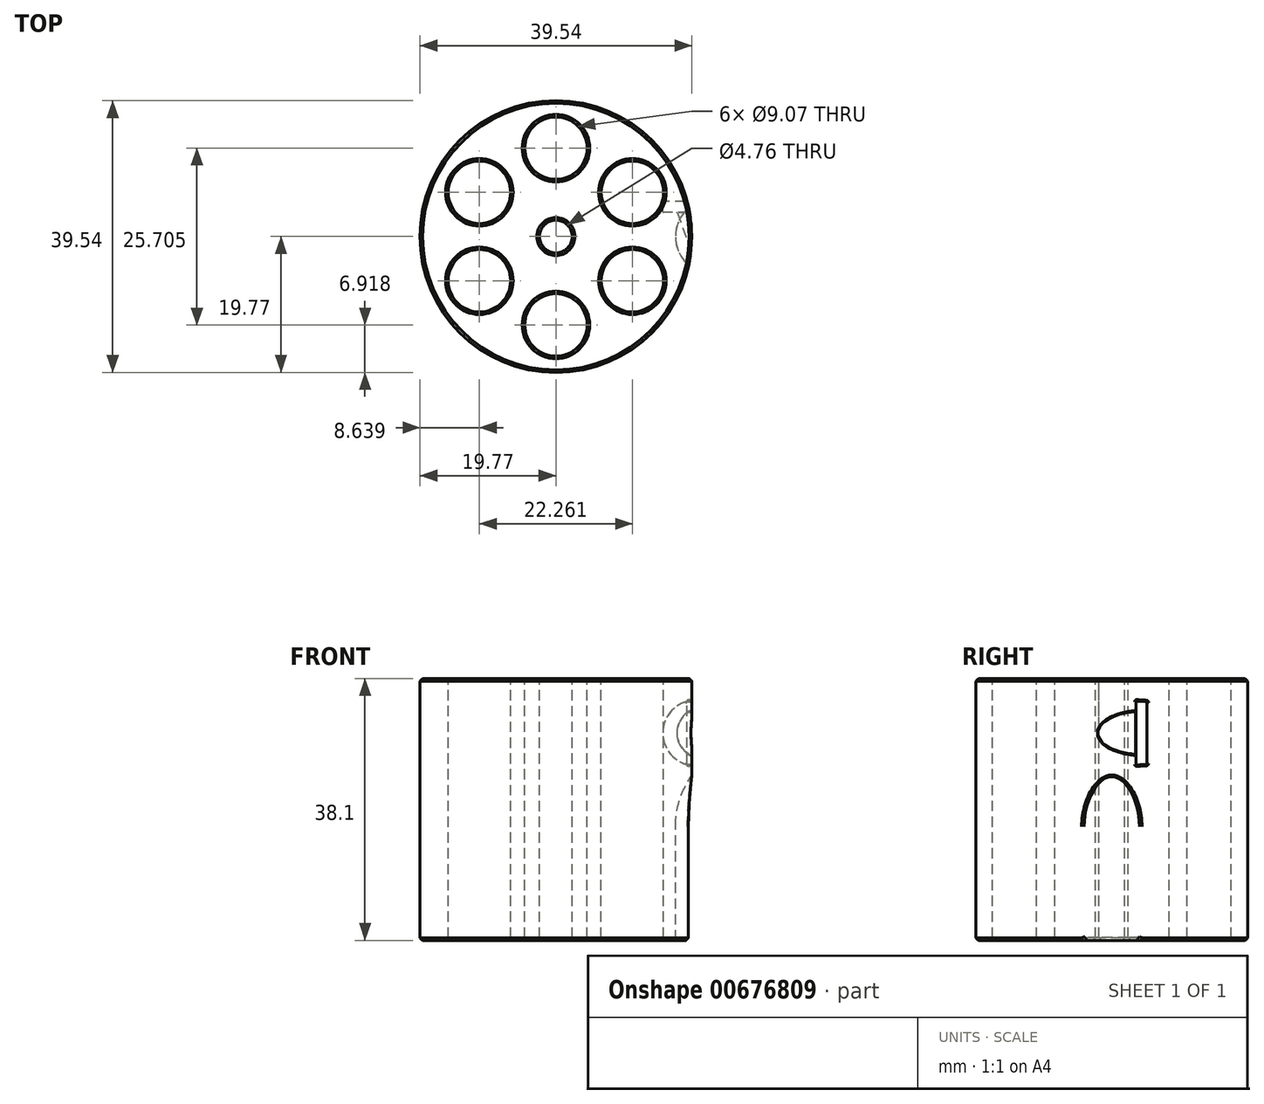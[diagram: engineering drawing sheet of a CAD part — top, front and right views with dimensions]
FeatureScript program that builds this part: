
annotation { "Feature Type Name" : "Feature", "Feature Type Description" : "" }
export const myFeature = defineFeature(function(context is Context, id is Id, definition is map)
    precondition{}
    {
        {
            var Q0;
            Q0=qCreatedBy(makeId("Top.planeOp"),FACE);
            var sketch = newSketch(context, id + "F0", { "sketchPlane" : qUnion([Q0])});
            skCircle(sketch, "E0", {"center": v(0, 0) * mm, "radius": 19.77 * mm});
            skCircle(sketch, "E1", {"center": v(0, 12.85) * mm, "radius": 4.53 * mm});
            skCircle(sketch, "E2", {"center": v(0, 0) * mm, "radius": 12.85 * mm, "construction": true});
            skCircle(sketch, "E3.1.0", {"center": v(-11.13, 6.43) * mm, "radius": 4.53 * mm});
            skCircle(sketch, "E3.2.0", {"center": v(-11.13, -6.43) * mm, "radius": 4.53 * mm});
            skCircle(sketch, "E4.1.3.0", {"center": v(0, -12.85) * mm, "radius": 4.53 * mm});
            skCircle(sketch, "E4.1.4.0", {"center": v(11.13, -6.43) * mm, "radius": 4.53 * mm});
            skCircle(sketch, "E4.1.5.0", {"center": v(11.13, 6.43) * mm, "radius": 4.53 * mm});
            skCircle(sketch, "E5", {"center": v(0, 18.58) * mm, "radius": 1.2 * mm, "construction": true});
            skCircle(sketch, "E6", {"center": v(0, 0) * mm, "radius": 2.38 * mm});
            skSolve(sketch);
        }
        {
            var Q0;
            Q0 = qSketchRegion(id + "F0", true);
            extrude(context, id + "F1", {"entities" : qUnion([Q0]), "oppositeDirection" : true, "depth" : 38.1 * mm, "offsetDistance" : 25.4 * mm});
        }
        {
            var Q0;
            Q0=makeQuery(id+"F1.opExtrude","CAP_EDGE",EDGE,{"disambiguationData":[OSD([sQuery(id+"F0.wireOp",EDGE,"E0")])],"isStart":true});
            var Q1;
            Q1=makeQuery(id+"F1.opExtrude","CAP_EDGE",EDGE,{"disambiguationData":[OSD([sQuery(id+"F0.wireOp",EDGE,"E0")])],"isStart":false});
            chamfer(context, id + "F2", {"entities" : qUnion([Q0, Q1]), "width" : 0.38 * mm, "tangentPropagation" : true});
        }
        {
            var Q0;
            Q0=makeQuery(id+"F1.opExtrude","CAP_EDGE",EDGE,{"disambiguationData":[OSD([sQuery(id+"F0.wireOp",EDGE,"E1")])],"isStart":false});
            var Q1;
            Q1=makeQuery(id+"F1.opExtrude","CAP_EDGE",EDGE,{"disambiguationData":[OSD([sQuery(id+"F0.wireOp",EDGE,"E3.1.0")])],"isStart":false});
            var Q2;
            Q2=makeQuery(id+"F1.opExtrude","CAP_EDGE",EDGE,{"disambiguationData":[OSD([sQuery(id+"F0.wireOp",EDGE,"E3.2.0")])],"isStart":false});
            var Q3;
            Q3=makeQuery(id+"F1.opExtrude","CAP_EDGE",EDGE,{"disambiguationData":[OSD([sQuery(id+"F0.wireOp",EDGE,"E4.1.3.0")])],"isStart":false});
            var Q4;
            Q4=makeQuery(id+"F1.opExtrude","CAP_EDGE",EDGE,{"disambiguationData":[OSD([sQuery(id+"F0.wireOp",EDGE,"E4.1.4.0")])],"isStart":false});
            var Q5;
            Q5=makeQuery(id+"F1.opExtrude","CAP_EDGE",EDGE,{"disambiguationData":[OSD([sQuery(id+"F0.wireOp",EDGE,"E4.1.5.0")])],"isStart":false});
            chamfer(context, id + "F3", {"entities" : qUnion([Q0, Q1, Q2, Q3, Q4, Q5]), "width" : 0.4 * mm, "tangentPropagation" : true});
        }
        {
            var Q0;
            Q0=makeQuery(id+"F1.opExtrude","CAP_EDGE",EDGE,{"disambiguationData":[OSD([sQuery(id+"F0.wireOp",EDGE,"E6")])],"isStart":true});
            var Q1;
            Q1=makeQuery(id+"F1.opExtrude","CAP_EDGE",EDGE,{"disambiguationData":[OSD([sQuery(id+"F0.wireOp",EDGE,"E6")])],"isStart":false});
            chamfer(context, id + "F4", {"entities" : qUnion([Q0, Q1]), "width" : 0.4 * mm, "tangentPropagation" : true});
        }
        {
            var Q0;
            Q0=qCreatedBy(makeId("Front.planeOp"),FACE);
            var sketch = newSketch(context, id + "F5", { "sketchPlane" : qUnion([Q0])});
            skLineSegment(sketch, "E7", {"start": v(22.86, -38.1) * mm, "end": v(17.4, -38.1) * mm});
            skLineSegment(sketch, "E8", {"start": v(17.4, -38.1) * mm, "end": v(17.4, -21.55) * mm});
            skLineSegment(sketch, "E9", {"start": v(22.86, -11.11) * mm, "end": v(17.4, -11.11) * mm, "construction": true});
            skArc(sketch, "E10", {"start": v(22.86, -11.11) * mm, "mid": v(18.85, -15.66) * mm, "end": v(17.4, -21.55) * mm});
            skLineSegment(sketch, "E11", {"start": v(22.86, -38.1) * mm, "end": v(22.86, -11.11) * mm});
            skLineSegment(sketch, "E12", {"start": v(0, 0) * mm, "end": v(0, -31.77) * mm, "construction": true});
            skSolve(sketch);
        }
        {
            var Q0;
            Q0=makeQuery(id+"F5.imprint","IMPRINT",FACE,{"disambiguationData":[TD([[makeQuery(id+"F5.imprint","IMPRINT",EDGE,{"derivedFrom":sQuery(id+"F5.wireOp",EDGE,"E7")}),-1.0]])]});
            var Q1;
            Q1=sQuery(id+"F5.wireOp",EDGE,"E11");
            revolve(context, id + "F6", {"operationType" : NewBodyOperationType.REMOVE, "entities" : qUnion([Q0]), "axis" : qUnion([Q1]), "revolveType" : RevolveType.FULL, "oppositeDirection" : true});
        }
        {
            var Q0;
            Q0=makeQuery(id+"F6.boolean.opBoolean","INTERSECT",EDGE,{"disambiguationData":[OD(1.0)],"derivedFrom":[makeQuery(id+"F1.opExtrude","SWEPT_FACE",FACE,{"disambiguationData":[OSD([sQuery(id+"F0.wireOp",EDGE,"E0")])]}),makeQuery(id+"F6.opRevolve","SWEPT_FACE",FACE,{"disambiguationData":[OSD([sQuery(id+"F5.wireOp",EDGE,"E8")])]})]});
            var Q1;
            Q1=makeQuery(id+"F6.boolean.opBoolean","COPY",EDGE,{"derivedFrom":makeQuery(id+"F6.opRevolve","SWEPT_EDGE",EDGE,{"disambiguationData":[OSD([sQuery(id+"F5.wireOp",EDGE,"E7"),sQuery(id+"F5.wireOp",EDGE,"E8")])]})});
            var Q2;
            {var subQ0=sQuery(id+"F0.wireOp",EDGE,"E0");Q2=makeQuery(id+"F6.boolean.opBoolean","INTERSECT",EDGE,{"disambiguationData":[OD(1.0)],"derivedFrom":[makeQuery(id+"F2.opChamfer","BLEND_FACE",FACE,{"disambiguationData":[OSD([subQ0]),TDD([makeQuery(id+"F1.opExtrude","CAP_EDGE",EDGE,{"disambiguationData":[OSD([subQ0])],"isStart":false})])]}),makeQuery(id+"F6.opRevolve","SWEPT_FACE",FACE,{"disambiguationData":[OSD([sQuery(id+"F5.wireOp",EDGE,"E8")])]})]});}
            var Q3;
            {var subQ0=sQuery(id+"F0.wireOp",EDGE,"E0");Q3=makeQuery(id+"F6.boolean.opBoolean","INTERSECT",EDGE,{"disambiguationData":[OD(0.0)],"derivedFrom":[makeQuery(id+"F2.opChamfer","BLEND_FACE",FACE,{"disambiguationData":[OSD([subQ0]),TDD([makeQuery(id+"F1.opExtrude","CAP_EDGE",EDGE,{"disambiguationData":[OSD([subQ0])],"isStart":false})])]}),makeQuery(id+"F6.opRevolve","SWEPT_FACE",FACE,{"disambiguationData":[OSD([sQuery(id+"F5.wireOp",EDGE,"E8")])]})]});}
            fillet(context, id + "F7", {"entities" : qUnion([Q0, Q1, Q2, Q3]), "radius" : 0.4 * mm, "tangentPropagation" : true, "allowEdgeOverflow" : false});
        }
        {
            var Q0;
            Q0=qCreatedBy(makeId("Front.planeOp"),FACE);
            cPlane(context, id + "F8", {"entities" : qUnion([Q0]), "cplaneType" : CPlaneType.OFFSET, "offset" : 5.08 * mm, "oppositeDirection" : true, "width" : 152.4 * mm, "height" : 152.4 * mm});
        }
        {
            var Q0;
            Q0=qCreatedBy(id+"F8.planeOp",FACE);
            var sketch = newSketch(context, id + "F9", { "sketchPlane" : qUnion([Q0])});
            skCircle(sketch, "E13", {"center": v(20.32, -7.94) * mm, "radius": 4.76 * mm});
            skLineSegment(sketch, "E14", {"start": v(0, 0) * mm, "end": v(0, -38.38) * mm, "construction": true});
            skSolve(sketch);
        }
        {
            var Q0;
            Q0=makeQuery(id+"F9.imprint","IMPRINT",FACE,{"disambiguationData":[TD([[makeQuery(id+"F9.imprint","IMPRINT",EDGE,{"derivedFrom":sQuery(id+"F9.wireOp",EDGE,"E13")}),1.0]])]});
            extrude(context, id + "F10", {"entities" : qUnion([Q0]), "operationType" : NewBodyOperationType.REMOVE, "depth" : 1.59 * mm, "offsetDistance" : 25.4 * mm});
        }
        {
            var Q0;
            Q0=makeQuery(id+"F10.boolean.opBoolean","INTERSECT",EDGE,{"derivedFrom":[makeQuery(id+"F1.opExtrude","SWEPT_FACE",FACE,{"disambiguationData":[OSD([sQuery(id+"F0.wireOp",EDGE,"E0")])]}),makeQuery(id+"F10.opExtrude","CAP_FACE",FACE,{"disambiguationData":[OSD([sQuery(id+"F9.wireOp",EDGE,"E13")])],"isStart":true})]});
            cPoint(context, id + "F11", {"entities" : qUnion([Q0]), "parameter" : 0.5});
        }
        {
            var Q0;
            Q0=makeQuery(id+"F1.opExtrude","CAP_FACE",FACE,{"disambiguationData":[OSD([sQuery(id+"F0.wireOp",EDGE,"E0"),sQuery(id+"F0.wireOp",EDGE,"E1"),sQuery(id+"F0.wireOp",EDGE,"E3.1.0"),sQuery(id+"F0.wireOp",EDGE,"E3.2.0"),sQuery(id+"F0.wireOp",EDGE,"E4.1.3.0"),sQuery(id+"F0.wireOp",EDGE,"E4.1.4.0"),sQuery(id+"F0.wireOp",EDGE,"E4.1.5.0"),sQuery(id+"F0.wireOp",EDGE,"E6")])],"isStart":true});
            var Q1;
            Q1 = qCreatedBy(id + "F11" ,VERTEX);
            cPlane(context, id + "F12", {"entities" : qUnion([Q0, Q1]), "cplaneType" : CPlaneType.PLANE_POINT, "offset" : 25.4 * mm, "width" : 152.4 * mm, "height" : 152.4 * mm});
        }
        {
            var Q0;
            Q0=qCreatedBy(id+"F12.planeOp",FACE);
            var sketch = newSketch(context, id + "F13", { "sketchPlane" : qUnion([Q0])});
            skLineSegment(sketch, "E15", {"start": v(20.98, 5.49) * mm, "end": v(27.05, -11.2) * mm});
            skLineSegment(sketch, "E16", {"start": v(27.05, -11.2) * mm, "end": v(23.47, -12.5) * mm});
            skLineSegment(sketch, "E17", {"start": v(23.47, -12.5) * mm, "end": v(17.4, 4.19) * mm});
            skLineSegment(sketch, "E18", {"start": v(0, 0) * mm, "end": v(8.72, -23.96) * mm, "construction": true});
            skLineSegment(sketch, "E19", {"start": v(13.64, 25.66) * mm, "end": v(31.2, -22.6) * mm, "construction": true});
            skLineSegment(sketch, "E20", {"start": v(0, 0) * mm, "end": v(0, -23.9) * mm, "construction": true});
            skLineSegment(sketch, "E21", {"start": v(17.4, 4.19) * mm, "end": v(20.98, 5.49) * mm});
            skSolve(sketch);
        }
        {
            var Q0;
            Q0 = qSketchRegion(id + "F13", true);
            var Q1;
            Q1=sQuery(id+"F13.wireOp",EDGE,"E19");
            revolve(context, id + "F14", {"operationType" : NewBodyOperationType.REMOVE, "entities" : qUnion([Q0]), "axis" : qUnion([Q1]), "revolveType" : RevolveType.FULL, "oppositeDirection" : true});
        }
        {
            var Q0;
            Q0=makeQuery(id+"F10.boolean.opBoolean","COPY",EDGE,{"derivedFrom":makeQuery(id+"F10.opExtrude","CAP_EDGE",EDGE,{"disambiguationData":[OSD([sQuery(id+"F9.wireOp",EDGE,"E13")])],"isStart":false})});
            var Q1;
            Q1=makeQuery(id+"F10.boolean.opBoolean","COPY",EDGE,{"derivedFrom":makeQuery(id+"F10.opExtrude","CAP_EDGE",EDGE,{"disambiguationData":[OSD([sQuery(id+"F9.wireOp",EDGE,"E13")])],"isStart":true})});
            var Q2;
            Q2=makeQuery(id+"F76gFO9HYB4MlWN_1.5.F10.boolean.opBoolean","COPY",EDGE,{"derivedFrom":makeQuery(id+"F76gFO9HYB4MlWN_1.5.F10.opExtrude","CAP_EDGE",EDGE,{"disambiguationData":[OSD([sQuery(id+"F9.wireOp",EDGE,"E13")])],"isStart":false})});
            var Q3;
            Q3=makeQuery(id+"F76gFO9HYB4MlWN_1.5.F10.boolean.opBoolean","COPY",EDGE,{"derivedFrom":makeQuery(id+"F76gFO9HYB4MlWN_1.5.F10.opExtrude","CAP_EDGE",EDGE,{"disambiguationData":[OSD([sQuery(id+"F9.wireOp",EDGE,"E13")])],"isStart":true})});
            var Q4;
            Q4=makeQuery(id+"F76gFO9HYB4MlWN_1.4.F10.boolean.opBoolean","COPY",EDGE,{"derivedFrom":makeQuery(id+"F76gFO9HYB4MlWN_1.4.F10.opExtrude","CAP_EDGE",EDGE,{"disambiguationData":[OSD([sQuery(id+"F9.wireOp",EDGE,"E13")])],"isStart":false})});
            var Q5;
            Q5=makeQuery(id+"F76gFO9HYB4MlWN_1.4.F10.boolean.opBoolean","COPY",EDGE,{"derivedFrom":makeQuery(id+"F76gFO9HYB4MlWN_1.4.F10.opExtrude","CAP_EDGE",EDGE,{"disambiguationData":[OSD([sQuery(id+"F9.wireOp",EDGE,"E13")])],"isStart":true})});
            var Q6;
            Q6=makeQuery(id+"F76gFO9HYB4MlWN_1.3.F10.boolean.opBoolean","COPY",EDGE,{"derivedFrom":makeQuery(id+"F76gFO9HYB4MlWN_1.3.F10.opExtrude","CAP_EDGE",EDGE,{"disambiguationData":[OSD([sQuery(id+"F9.wireOp",EDGE,"E13")])],"isStart":false})});
            var Q7;
            Q7=makeQuery(id+"F76gFO9HYB4MlWN_1.3.F10.boolean.opBoolean","COPY",EDGE,{"derivedFrom":makeQuery(id+"F76gFO9HYB4MlWN_1.3.F10.opExtrude","CAP_EDGE",EDGE,{"disambiguationData":[OSD([sQuery(id+"F9.wireOp",EDGE,"E13")])],"isStart":true})});
            var Q8;
            Q8=makeQuery(id+"F76gFO9HYB4MlWN_1.2.F10.boolean.opBoolean","COPY",EDGE,{"derivedFrom":makeQuery(id+"F76gFO9HYB4MlWN_1.2.F10.opExtrude","CAP_EDGE",EDGE,{"disambiguationData":[OSD([sQuery(id+"F9.wireOp",EDGE,"E13")])],"isStart":false})});
            var Q9;
            Q9=makeQuery(id+"F76gFO9HYB4MlWN_1.2.F10.boolean.opBoolean","COPY",EDGE,{"derivedFrom":makeQuery(id+"F76gFO9HYB4MlWN_1.2.F10.opExtrude","CAP_EDGE",EDGE,{"disambiguationData":[OSD([sQuery(id+"F9.wireOp",EDGE,"E13")])],"isStart":true})});
            var Q10;
            Q10=makeQuery(id+"F76gFO9HYB4MlWN_1.1.F10.boolean.opBoolean","COPY",EDGE,{"derivedFrom":makeQuery(id+"F76gFO9HYB4MlWN_1.1.F10.opExtrude","CAP_EDGE",EDGE,{"disambiguationData":[OSD([sQuery(id+"F9.wireOp",EDGE,"E13")])],"isStart":false})});
            var Q11;
            Q11=makeQuery(id+"F76gFO9HYB4MlWN_1.1.F10.boolean.opBoolean","COPY",EDGE,{"derivedFrom":makeQuery(id+"F76gFO9HYB4MlWN_1.1.F10.opExtrude","CAP_EDGE",EDGE,{"disambiguationData":[OSD([sQuery(id+"F9.wireOp",EDGE,"E13")])],"isStart":true})});
            var Q12;
            Q12=makeQuery(id+"Fe7n6pQzUNQBplN_1.1.F14.boolean.opBoolean","INTERSECT",EDGE,{"derivedFrom":[makeQuery(id+"F76gFO9HYB4MlWN_1.1.F10.boolean.opBoolean","COPY",FACE,{"derivedFrom":makeQuery(id+"F76gFO9HYB4MlWN_1.1.F10.opExtrude","CAP_FACE",FACE,{"disambiguationData":[OSD([sQuery(id+"F9.wireOp",EDGE,"E13")])],"isStart":false})}),makeQuery(id+"Fe7n6pQzUNQBplN_1.1.F14.opRevolve","SWEPT_FACE",FACE,{"disambiguationData":[OSD([sQuery(id+"F13.wireOp",EDGE,"E17")])]})]});
            var Q13;
            Q13=makeQuery(id+"Fe7n6pQzUNQBplN_1.2.F14.boolean.opBoolean","INTERSECT",EDGE,{"derivedFrom":[makeQuery(id+"F76gFO9HYB4MlWN_1.2.F10.boolean.opBoolean","COPY",FACE,{"derivedFrom":makeQuery(id+"F76gFO9HYB4MlWN_1.2.F10.opExtrude","CAP_FACE",FACE,{"disambiguationData":[OSD([sQuery(id+"F9.wireOp",EDGE,"E13")])],"isStart":false})}),makeQuery(id+"Fe7n6pQzUNQBplN_1.2.F14.opRevolve","SWEPT_FACE",FACE,{"disambiguationData":[OSD([sQuery(id+"F13.wireOp",EDGE,"E17")])]})]});
            var Q14;
            Q14=makeQuery(id+"F14.boolean.opBoolean","INTERSECT",EDGE,{"derivedFrom":[makeQuery(id+"F10.boolean.opBoolean","COPY",FACE,{"derivedFrom":makeQuery(id+"F10.opExtrude","CAP_FACE",FACE,{"disambiguationData":[OSD([sQuery(id+"F9.wireOp",EDGE,"E13")])],"isStart":false})}),makeQuery(id+"F14.opRevolve","SWEPT_FACE",FACE,{"disambiguationData":[OSD([sQuery(id+"F13.wireOp",EDGE,"E17")])]})]});
            var Q15;
            Q15=makeQuery(id+"Fe7n6pQzUNQBplN_1.3.F14.boolean.opBoolean","INTERSECT",EDGE,{"derivedFrom":[makeQuery(id+"F76gFO9HYB4MlWN_1.3.F10.boolean.opBoolean","COPY",FACE,{"derivedFrom":makeQuery(id+"F76gFO9HYB4MlWN_1.3.F10.opExtrude","CAP_FACE",FACE,{"disambiguationData":[OSD([sQuery(id+"F9.wireOp",EDGE,"E13")])],"isStart":false})}),makeQuery(id+"Fe7n6pQzUNQBplN_1.3.F14.opRevolve","SWEPT_FACE",FACE,{"disambiguationData":[OSD([sQuery(id+"F13.wireOp",EDGE,"E17")])]})]});
            var Q16;
            Q16=makeQuery(id+"Fe7n6pQzUNQBplN_1.4.F14.boolean.opBoolean","INTERSECT",EDGE,{"derivedFrom":[makeQuery(id+"F76gFO9HYB4MlWN_1.4.F10.boolean.opBoolean","COPY",FACE,{"derivedFrom":makeQuery(id+"F76gFO9HYB4MlWN_1.4.F10.opExtrude","CAP_FACE",FACE,{"disambiguationData":[OSD([sQuery(id+"F9.wireOp",EDGE,"E13")])],"isStart":false})}),makeQuery(id+"Fe7n6pQzUNQBplN_1.4.F14.opRevolve","SWEPT_FACE",FACE,{"disambiguationData":[OSD([sQuery(id+"F13.wireOp",EDGE,"E17")])]})]});
            var Q17;
            Q17=makeQuery(id+"Fe7n6pQzUNQBplN_1.5.F14.boolean.opBoolean","INTERSECT",EDGE,{"derivedFrom":[makeQuery(id+"F76gFO9HYB4MlWN_1.5.F10.boolean.opBoolean","COPY",FACE,{"derivedFrom":makeQuery(id+"F76gFO9HYB4MlWN_1.5.F10.opExtrude","CAP_FACE",FACE,{"disambiguationData":[OSD([sQuery(id+"F9.wireOp",EDGE,"E13")])],"isStart":false})}),makeQuery(id+"Fe7n6pQzUNQBplN_1.5.F14.opRevolve","SWEPT_FACE",FACE,{"disambiguationData":[OSD([sQuery(id+"F13.wireOp",EDGE,"E17")])]})]});
            fillet(context, id + "F15", {"entities" : qUnion([Q0, Q1, Q2, Q3, Q4, Q5, Q6, Q7, Q8, Q9, Q10, Q11, Q12, Q13, Q14, Q15, Q16, Q17]), "radius" : 0.08 * mm, "tangentPropagation" : true, "allowEdgeOverflow" : false});
        }
        {
            var Q0;
            Q0=makeQuery(id+"F14.boolean.opBoolean","INTERSECT",EDGE,{"derivedFrom":[makeQuery(id+"F1.opExtrude","SWEPT_FACE",FACE,{"disambiguationData":[OSD([sQuery(id+"F0.wireOp",EDGE,"E0")])]}),makeQuery(id+"F14.opRevolve","SWEPT_FACE",FACE,{"disambiguationData":[OSD([sQuery(id+"F13.wireOp",EDGE,"E17")])]})]});
            var Q1;
            Q1=makeQuery(id+"Fe7n6pQzUNQBplN_1.5.F14.boolean.opBoolean","INTERSECT",EDGE,{"derivedFrom":[makeQuery(id+"F1.opExtrude","SWEPT_FACE",FACE,{"disambiguationData":[OSD([sQuery(id+"F0.wireOp",EDGE,"E0")])]}),makeQuery(id+"Fe7n6pQzUNQBplN_1.5.F14.opRevolve","SWEPT_FACE",FACE,{"disambiguationData":[OSD([sQuery(id+"F13.wireOp",EDGE,"E17")])]})]});
            var Q2;
            Q2=makeQuery(id+"Fe7n6pQzUNQBplN_1.1.F14.boolean.opBoolean","INTERSECT",EDGE,{"derivedFrom":[makeQuery(id+"F1.opExtrude","SWEPT_FACE",FACE,{"disambiguationData":[OSD([sQuery(id+"F0.wireOp",EDGE,"E0")])]}),makeQuery(id+"Fe7n6pQzUNQBplN_1.1.F14.opRevolve","SWEPT_FACE",FACE,{"disambiguationData":[OSD([sQuery(id+"F13.wireOp",EDGE,"E17")])]})]});
            var Q3;
            Q3=makeQuery(id+"Fe7n6pQzUNQBplN_1.4.F14.boolean.opBoolean","INTERSECT",EDGE,{"derivedFrom":[makeQuery(id+"F1.opExtrude","SWEPT_FACE",FACE,{"disambiguationData":[OSD([sQuery(id+"F0.wireOp",EDGE,"E0")])]}),makeQuery(id+"Fe7n6pQzUNQBplN_1.4.F14.opRevolve","SWEPT_FACE",FACE,{"disambiguationData":[OSD([sQuery(id+"F13.wireOp",EDGE,"E17")])]})]});
            var Q4;
            Q4=makeQuery(id+"Fe7n6pQzUNQBplN_1.3.F14.boolean.opBoolean","INTERSECT",EDGE,{"derivedFrom":[makeQuery(id+"F1.opExtrude","SWEPT_FACE",FACE,{"disambiguationData":[OSD([sQuery(id+"F0.wireOp",EDGE,"E0")])]}),makeQuery(id+"Fe7n6pQzUNQBplN_1.3.F14.opRevolve","SWEPT_FACE",FACE,{"disambiguationData":[OSD([sQuery(id+"F13.wireOp",EDGE,"E17")])]})]});
            var Q5;
            Q5=makeQuery(id+"Fe7n6pQzUNQBplN_1.2.F14.boolean.opBoolean","INTERSECT",EDGE,{"derivedFrom":[makeQuery(id+"F1.opExtrude","SWEPT_FACE",FACE,{"disambiguationData":[OSD([sQuery(id+"F0.wireOp",EDGE,"E0")])]}),makeQuery(id+"Fe7n6pQzUNQBplN_1.2.F14.opRevolve","SWEPT_FACE",FACE,{"disambiguationData":[OSD([sQuery(id+"F13.wireOp",EDGE,"E17")])]})]});
            fillet(context, id + "F16", {"entities" : qUnion([Q0, Q1, Q2, Q3, Q4, Q5]), "radius" : 0.2 * mm, "tangentPropagation" : true, "allowEdgeOverflow" : false});
        }
        {
            var Q0;
            Q0=makeQuery(id+"F1.opExtrude","CAP_EDGE",EDGE,{"disambiguationData":[OSD([sQuery(id+"F0.wireOp",EDGE,"E1")])],"isStart":true});
            var Q1;
            Q1=makeQuery(id+"F1.opExtrude","CAP_EDGE",EDGE,{"disambiguationData":[OSD([sQuery(id+"F0.wireOp",EDGE,"E4.1.5.0")])],"isStart":true});
            var Q2;
            Q2=makeQuery(id+"F1.opExtrude","CAP_EDGE",EDGE,{"disambiguationData":[OSD([sQuery(id+"F0.wireOp",EDGE,"E4.1.4.0")])],"isStart":true});
            var Q3;
            Q3=makeQuery(id+"F1.opExtrude","CAP_EDGE",EDGE,{"disambiguationData":[OSD([sQuery(id+"F0.wireOp",EDGE,"E4.1.3.0")])],"isStart":true});
            var Q4;
            Q4=makeQuery(id+"F1.opExtrude","CAP_EDGE",EDGE,{"disambiguationData":[OSD([sQuery(id+"F0.wireOp",EDGE,"E3.2.0")])],"isStart":true});
            var Q5;
            Q5=makeQuery(id+"F1.opExtrude","CAP_EDGE",EDGE,{"disambiguationData":[OSD([sQuery(id+"F0.wireOp",EDGE,"E3.1.0")])],"isStart":true});
            chamfer(context, id + "F17", {"entities" : qUnion([Q0, Q1, Q2, Q3, Q4, Q5]), "width" : 0.38 * mm, "tangentPropagation" : true});
        }
    });
